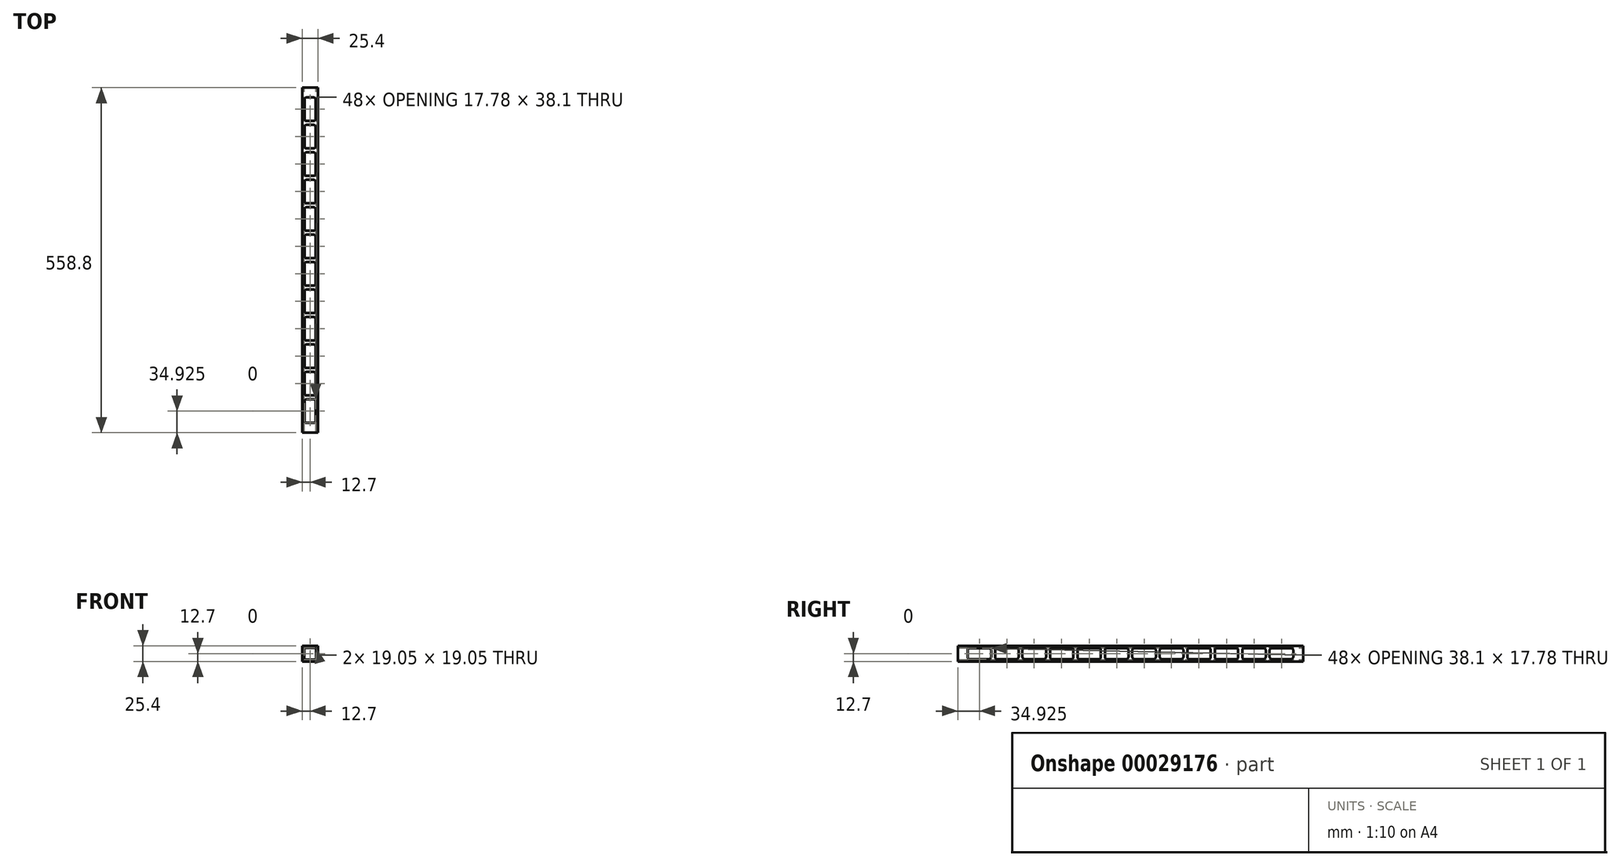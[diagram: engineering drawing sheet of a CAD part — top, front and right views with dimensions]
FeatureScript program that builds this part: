
annotation { "Feature Type Name" : "Feature", "Feature Type Description" : "" }
export const myFeature = defineFeature(function(context is Context, id is Id, definition is map)
    precondition{}
    {
        {
            var Q0;
            Q0=qCreatedBy(makeId("Front.planeOp"),FACE);
            var sketch = newSketch(context, id + "F0", { "sketchPlane" : qUnion([Q0])});
            skLineSegment(sketch, "E0.rect.bottom", {"start": v(12.7, 12.7) * mm, "end": v(-12.7, 12.7) * mm});
            skLineSegment(sketch, "E0.rect.top", {"start": v(12.7, -12.7) * mm, "end": v(-12.7, -12.7) * mm});
            skLineSegment(sketch, "E0.rect.left", {"start": v(12.7, 12.7) * mm, "end": v(12.7, -12.7) * mm});
            skLineSegment(sketch, "E0.rect.right", {"start": v(-12.7, 12.7) * mm, "end": v(-12.7, -12.7) * mm});
            skPoint(sketch, "E0.rect.middle", {"position": v(0, 0) * mm});
            skLineSegment(sketch, "E1.rect.bottom", {"start": v(9.53, 9.53) * mm, "end": v(-9.53, 9.53) * mm});
            skLineSegment(sketch, "E1.rect.top", {"start": v(9.53, -9.53) * mm, "end": v(-9.53, -9.53) * mm});
            skLineSegment(sketch, "E1.rect.left", {"start": v(9.53, 9.53) * mm, "end": v(9.53, -9.53) * mm});
            skLineSegment(sketch, "E1.rect.right", {"start": v(-9.53, 9.53) * mm, "end": v(-9.53, -9.53) * mm});
            skSolve(sketch);
        }
        {
            var Q0;
            Q0=qSketchRegion(id+"F0",true);
            extrude(context, id + "F1", {"entities" : qUnion([Q0]), "depth" : 558.8 * mm});
        }
        {
            var Q0;
            Q0=makeQuery(id+"F1.opExtrude","SWEPT_FACE",FACE,{"disambiguationData":[OSD([sQuery(id+"F0.wireOp",EDGE,"E0.rect.left")])]});
            var sketch = newSketch(context, id + "F2", { "sketchPlane" : qUnion([Q0])});
            skLineSegment(sketch, "E2", {"start": v(-558.8, 0) * mm, "end": v(-542.93, 0) * mm});
            skLineSegment(sketch, "E3.rect.bottom", {"start": v(-508, 8.89) * mm, "end": v(-539.75, 8.89) * mm});
            skLineSegment(sketch, "E3.rect.top", {"start": v(-508, -8.9) * mm, "end": v(-539.75, -8.9) * mm});
            skLineSegment(sketch, "E3.rect.left", {"start": v(-504.83, 5.71) * mm, "end": v(-504.83, -5.72) * mm});
            skLineSegment(sketch, "E3.rect.right", {"start": v(-542.93, 5.71) * mm, "end": v(-542.93, -5.72) * mm});
            skPoint(sketch, "E3.rect.middle", {"position": v(-523.88, 0) * mm});
            skPoint(sketch, "E4.visualSharp", {"position": v(-504.83, 8.89) * mm});
            skArc(sketch, "E4.filletArc", {"start": v(-504.83, 5.71) * mm, "mid": v(-505.75, 7.96) * mm, "end": v(-508, 8.89) * mm});
            skPoint(sketch, "E5.visualSharp", {"position": v(-504.83, -8.9) * mm});
            skArc(sketch, "E5.filletArc", {"start": v(-508, -8.9) * mm, "mid": v(-505.75, -7.96) * mm, "end": v(-504.82, -5.72) * mm});
            skPoint(sketch, "E6.visualSharp", {"position": v(-542.93, -8.9) * mm});
            skArc(sketch, "E6.filletArc", {"start": v(-542.93, -5.72) * mm, "mid": v(-542, -7.96) * mm, "end": v(-539.75, -8.9) * mm});
            skPoint(sketch, "E7.visualSharp", {"position": v(-542.93, 8.89) * mm});
            skArc(sketch, "E7.filletArc", {"start": v(-539.75, 8.9) * mm, "mid": v(-542, 7.96) * mm, "end": v(-542.93, 5.71) * mm});
            skLineSegment(sketch, "E8.1.0.0", {"start": v(-460.38, 5.71) * mm, "end": v(-460.38, -5.72) * mm});
            skArc(sketch, "E8.1.0.1", {"start": v(-460.38, 5.71) * mm, "mid": v(-461.3, 7.96) * mm, "end": v(-463.55, 8.89) * mm});
            skLineSegment(sketch, "E8.1.0.2", {"start": v(-463.55, 8.89) * mm, "end": v(-495.3, 8.89) * mm});
            skArc(sketch, "E8.1.0.3", {"start": v(-495.3, 8.9) * mm, "mid": v(-497.55, 7.96) * mm, "end": v(-498.48, 5.71) * mm});
            skLineSegment(sketch, "E8.1.0.4", {"start": v(-498.48, 5.71) * mm, "end": v(-498.48, -5.72) * mm});
            skArc(sketch, "E8.1.0.5", {"start": v(-498.48, -5.72) * mm, "mid": v(-497.55, -7.96) * mm, "end": v(-495.3, -8.9) * mm});
            skLineSegment(sketch, "E8.1.0.6", {"start": v(-463.55, -8.9) * mm, "end": v(-495.3, -8.9) * mm});
            skArc(sketch, "E8.1.0.7", {"start": v(-463.55, -8.9) * mm, "mid": v(-461.3, -7.96) * mm, "end": v(-460.38, -5.72) * mm});
            skLineSegment(sketch, "E8.2.0.0", {"start": v(-415.93, 5.71) * mm, "end": v(-415.93, -5.72) * mm});
            skArc(sketch, "E8.2.0.1", {"start": v(-415.93, 5.71) * mm, "mid": v(-416.85, 7.96) * mm, "end": v(-419.1, 8.89) * mm});
            skLineSegment(sketch, "E8.2.0.2", {"start": v(-419.1, 8.89) * mm, "end": v(-450.85, 8.89) * mm});
            skArc(sketch, "E8.2.0.3", {"start": v(-450.85, 8.9) * mm, "mid": v(-453.1, 7.96) * mm, "end": v(-454.03, 5.71) * mm});
            skLineSegment(sketch, "E8.2.0.4", {"start": v(-454.03, 5.71) * mm, "end": v(-454.03, -5.72) * mm});
            skArc(sketch, "E8.2.0.5", {"start": v(-454.03, -5.72) * mm, "mid": v(-453.1, -7.96) * mm, "end": v(-450.85, -8.9) * mm});
            skLineSegment(sketch, "E8.2.0.6", {"start": v(-419.1, -8.9) * mm, "end": v(-450.85, -8.9) * mm});
            skArc(sketch, "E8.2.0.7", {"start": v(-419.1, -8.9) * mm, "mid": v(-416.85, -7.96) * mm, "end": v(-415.93, -5.72) * mm});
            skLineSegment(sketch, "E8.3.0.0", {"start": v(-371.48, 5.71) * mm, "end": v(-371.48, -5.72) * mm});
            skArc(sketch, "E8.3.0.1", {"start": v(-371.48, 5.71) * mm, "mid": v(-372.4, 7.96) * mm, "end": v(-374.65, 8.89) * mm});
            skLineSegment(sketch, "E8.3.0.2", {"start": v(-374.65, 8.89) * mm, "end": v(-406.4, 8.89) * mm});
            skArc(sketch, "E8.3.0.3", {"start": v(-406.4, 8.9) * mm, "mid": v(-408.65, 7.96) * mm, "end": v(-409.58, 5.71) * mm});
            skLineSegment(sketch, "E8.3.0.4", {"start": v(-409.58, 5.71) * mm, "end": v(-409.58, -5.72) * mm});
            skArc(sketch, "E8.3.0.5", {"start": v(-409.58, -5.72) * mm, "mid": v(-408.65, -7.96) * mm, "end": v(-406.4, -8.9) * mm});
            skLineSegment(sketch, "E8.3.0.6", {"start": v(-374.65, -8.9) * mm, "end": v(-406.4, -8.9) * mm});
            skArc(sketch, "E8.3.0.7", {"start": v(-374.65, -8.9) * mm, "mid": v(-372.4, -7.96) * mm, "end": v(-371.48, -5.72) * mm});
            skLineSegment(sketch, "E8.4.0.0", {"start": v(-327.03, 5.71) * mm, "end": v(-327.03, -5.72) * mm});
            skArc(sketch, "E8.4.0.1", {"start": v(-327.03, 5.71) * mm, "mid": v(-327.95, 7.96) * mm, "end": v(-330.2, 8.89) * mm});
            skLineSegment(sketch, "E8.4.0.2", {"start": v(-330.2, 8.89) * mm, "end": v(-361.95, 8.89) * mm});
            skArc(sketch, "E8.4.0.3", {"start": v(-361.95, 8.9) * mm, "mid": v(-364.2, 7.96) * mm, "end": v(-365.13, 5.71) * mm});
            skLineSegment(sketch, "E8.4.0.4", {"start": v(-365.13, 5.71) * mm, "end": v(-365.13, -5.72) * mm});
            skArc(sketch, "E8.4.0.5", {"start": v(-365.13, -5.72) * mm, "mid": v(-364.2, -7.96) * mm, "end": v(-361.95, -8.9) * mm});
            skLineSegment(sketch, "E8.4.0.6", {"start": v(-330.2, -8.9) * mm, "end": v(-361.95, -8.9) * mm});
            skArc(sketch, "E8.4.0.7", {"start": v(-330.2, -8.9) * mm, "mid": v(-327.95, -7.96) * mm, "end": v(-327.03, -5.72) * mm});
            skLineSegment(sketch, "E8.5.0.0", {"start": v(-282.58, 5.71) * mm, "end": v(-282.58, -5.72) * mm});
            skArc(sketch, "E8.5.0.1", {"start": v(-282.58, 5.71) * mm, "mid": v(-283.5, 7.96) * mm, "end": v(-285.75, 8.89) * mm});
            skLineSegment(sketch, "E8.5.0.2", {"start": v(-285.75, 8.89) * mm, "end": v(-317.5, 8.89) * mm});
            skArc(sketch, "E8.5.0.3", {"start": v(-317.5, 8.9) * mm, "mid": v(-319.75, 7.96) * mm, "end": v(-320.68, 5.71) * mm});
            skLineSegment(sketch, "E8.5.0.4", {"start": v(-320.68, 5.71) * mm, "end": v(-320.68, -5.72) * mm});
            skArc(sketch, "E8.5.0.5", {"start": v(-320.68, -5.72) * mm, "mid": v(-319.75, -7.96) * mm, "end": v(-317.5, -8.9) * mm});
            skLineSegment(sketch, "E8.5.0.6", {"start": v(-285.75, -8.9) * mm, "end": v(-317.5, -8.9) * mm});
            skArc(sketch, "E8.5.0.7", {"start": v(-285.75, -8.9) * mm, "mid": v(-283.5, -7.96) * mm, "end": v(-282.58, -5.72) * mm});
            skLineSegment(sketch, "E8.6.0.0", {"start": v(-238.13, 5.71) * mm, "end": v(-238.13, -5.72) * mm});
            skArc(sketch, "E8.6.0.1", {"start": v(-238.13, 5.71) * mm, "mid": v(-239.05, 7.96) * mm, "end": v(-241.3, 8.89) * mm});
            skLineSegment(sketch, "E8.6.0.2", {"start": v(-241.3, 8.89) * mm, "end": v(-273.05, 8.89) * mm});
            skArc(sketch, "E8.6.0.3", {"start": v(-273.05, 8.9) * mm, "mid": v(-275.3, 7.96) * mm, "end": v(-276.23, 5.71) * mm});
            skLineSegment(sketch, "E8.6.0.4", {"start": v(-276.23, 5.71) * mm, "end": v(-276.23, -5.72) * mm});
            skArc(sketch, "E8.6.0.5", {"start": v(-276.23, -5.72) * mm, "mid": v(-275.3, -7.96) * mm, "end": v(-273.05, -8.9) * mm});
            skLineSegment(sketch, "E8.6.0.6", {"start": v(-241.3, -8.9) * mm, "end": v(-273.05, -8.9) * mm});
            skArc(sketch, "E8.6.0.7", {"start": v(-241.3, -8.9) * mm, "mid": v(-239.05, -7.96) * mm, "end": v(-238.13, -5.72) * mm});
            skLineSegment(sketch, "E8.7.0.0", {"start": v(-193.68, 5.71) * mm, "end": v(-193.68, -5.72) * mm});
            skArc(sketch, "E8.7.0.1", {"start": v(-193.68, 5.71) * mm, "mid": v(-194.6, 7.96) * mm, "end": v(-196.85, 8.89) * mm});
            skLineSegment(sketch, "E8.7.0.2", {"start": v(-196.85, 8.89) * mm, "end": v(-228.6, 8.89) * mm});
            skArc(sketch, "E8.7.0.3", {"start": v(-228.6, 8.9) * mm, "mid": v(-230.85, 7.96) * mm, "end": v(-231.78, 5.71) * mm});
            skLineSegment(sketch, "E8.7.0.4", {"start": v(-231.78, 5.71) * mm, "end": v(-231.78, -5.72) * mm});
            skArc(sketch, "E8.7.0.5", {"start": v(-231.78, -5.72) * mm, "mid": v(-230.85, -7.96) * mm, "end": v(-228.6, -8.9) * mm});
            skLineSegment(sketch, "E8.7.0.6", {"start": v(-196.85, -8.9) * mm, "end": v(-228.6, -8.9) * mm});
            skArc(sketch, "E8.7.0.7", {"start": v(-196.85, -8.9) * mm, "mid": v(-194.6, -7.96) * mm, "end": v(-193.68, -5.72) * mm});
            skLineSegment(sketch, "E8.8.0.0", {"start": v(-149.23, 5.71) * mm, "end": v(-149.23, -5.72) * mm});
            skArc(sketch, "E8.8.0.1", {"start": v(-149.23, 5.71) * mm, "mid": v(-150.15, 7.96) * mm, "end": v(-152.4, 8.89) * mm});
            skLineSegment(sketch, "E8.8.0.2", {"start": v(-152.4, 8.89) * mm, "end": v(-184.15, 8.89) * mm});
            skArc(sketch, "E8.8.0.3", {"start": v(-184.15, 8.9) * mm, "mid": v(-186.4, 7.96) * mm, "end": v(-187.33, 5.71) * mm});
            skLineSegment(sketch, "E8.8.0.4", {"start": v(-187.33, 5.71) * mm, "end": v(-187.33, -5.72) * mm});
            skArc(sketch, "E8.8.0.5", {"start": v(-187.33, -5.72) * mm, "mid": v(-186.4, -7.96) * mm, "end": v(-184.15, -8.9) * mm});
            skLineSegment(sketch, "E8.8.0.6", {"start": v(-152.4, -8.9) * mm, "end": v(-184.15, -8.9) * mm});
            skArc(sketch, "E8.8.0.7", {"start": v(-152.4, -8.9) * mm, "mid": v(-150.15, -7.96) * mm, "end": v(-149.23, -5.72) * mm});
            skLineSegment(sketch, "E8.direction1", {"start": v(-504.83, -5.72) * mm, "end": v(-460.38, -5.72) * mm, "construction": true});
            skLineSegment(sketch, "E9.0.9.0", {"start": v(-104.78, 5.71) * mm, "end": v(-104.78, -5.72) * mm});
            skArc(sketch, "E9.3.9.0", {"start": v(-104.78, 5.71) * mm, "mid": v(-105.7, 7.96) * mm, "end": v(-107.95, 8.89) * mm});
            skLineSegment(sketch, "E9.7.9.0", {"start": v(-107.95, 8.89) * mm, "end": v(-139.7, 8.89) * mm});
            skArc(sketch, "E9.10.9.0", {"start": v(-139.7, 8.9) * mm, "mid": v(-141.95, 7.96) * mm, "end": v(-142.88, 5.71) * mm});
            skLineSegment(sketch, "E9.14.9.0", {"start": v(-142.88, 5.71) * mm, "end": v(-142.88, -5.72) * mm});
            skArc(sketch, "E9.17.9.0", {"start": v(-142.88, -5.72) * mm, "mid": v(-141.95, -7.96) * mm, "end": v(-139.7, -8.9) * mm});
            skLineSegment(sketch, "E9.21.9.0", {"start": v(-107.95, -8.9) * mm, "end": v(-139.7, -8.9) * mm});
            skArc(sketch, "E9.24.9.0", {"start": v(-107.95, -8.9) * mm, "mid": v(-105.7, -7.96) * mm, "end": v(-104.78, -5.72) * mm});
            skLineSegment(sketch, "E9.0.10.0", {"start": v(-60.33, 5.71) * mm, "end": v(-60.33, -5.72) * mm});
            skArc(sketch, "E9.3.10.0", {"start": v(-60.33, 5.71) * mm, "mid": v(-61.25, 7.96) * mm, "end": v(-63.5, 8.89) * mm});
            skLineSegment(sketch, "E9.7.10.0", {"start": v(-63.5, 8.89) * mm, "end": v(-95.25, 8.89) * mm});
            skArc(sketch, "E9.10.10.0", {"start": v(-95.25, 8.9) * mm, "mid": v(-97.5, 7.96) * mm, "end": v(-98.43, 5.71) * mm});
            skLineSegment(sketch, "E9.14.10.0", {"start": v(-98.43, 5.71) * mm, "end": v(-98.43, -5.72) * mm});
            skArc(sketch, "E9.17.10.0", {"start": v(-98.43, -5.72) * mm, "mid": v(-97.5, -7.96) * mm, "end": v(-95.25, -8.9) * mm});
            skLineSegment(sketch, "E9.21.10.0", {"start": v(-63.5, -8.9) * mm, "end": v(-95.25, -8.9) * mm});
            skArc(sketch, "E9.24.10.0", {"start": v(-63.5, -8.9) * mm, "mid": v(-61.25, -7.96) * mm, "end": v(-60.33, -5.72) * mm});
            skLineSegment(sketch, "E10.0.11.0", {"start": v(-15.88, 5.71) * mm, "end": v(-15.88, -5.72) * mm});
            skArc(sketch, "E10.3.11.0", {"start": v(-15.88, 5.71) * mm, "mid": v(-16.8, 7.96) * mm, "end": v(-19.05, 8.89) * mm});
            skLineSegment(sketch, "E10.7.11.0", {"start": v(-19.05, 8.89) * mm, "end": v(-50.8, 8.89) * mm});
            skArc(sketch, "E10.10.11.0", {"start": v(-50.8, 8.9) * mm, "mid": v(-53.05, 7.96) * mm, "end": v(-53.98, 5.71) * mm});
            skLineSegment(sketch, "E10.14.11.0", {"start": v(-53.98, 5.71) * mm, "end": v(-53.98, -5.72) * mm});
            skArc(sketch, "E10.17.11.0", {"start": v(-53.98, -5.72) * mm, "mid": v(-53.05, -7.96) * mm, "end": v(-50.8, -8.9) * mm});
            skLineSegment(sketch, "E10.21.11.0", {"start": v(-19.05, -8.9) * mm, "end": v(-50.8, -8.9) * mm});
            skArc(sketch, "E10.24.11.0", {"start": v(-19.05, -8.9) * mm, "mid": v(-16.8, -7.96) * mm, "end": v(-15.88, -5.72) * mm});
            skLineSegment(sketch, "E11.trimOffspring", {"start": v(-504.83, 0) * mm, "end": v(0, 0) * mm});
            skSolve(sketch);
        }
        {
            var Q0;
            Q0 = qSketchRegion(id + "F2", true);
            extrude(context, id + "F3", {"entities" : qUnion([Q0]), "operationType" : NewBodyOperationType.REMOVE, "oppositeDirection" : true, "depth" : 25.4 * mm});
        }
        {
            var Q0;
            Q0=makeQuery(id+"F1.opExtrude","SWEPT_FACE",FACE,{"disambiguationData":[OSD([sQuery(id+"F0.wireOp",EDGE,"E0.rect.bottom")])]});
            var sketch = newSketch(context, id + "F4", { "sketchPlane" : qUnion([Q0])});
            skLineSegment(sketch, "E12", {"start": v(0, -558.8) * mm, "end": v(0, 0) * mm});
            skLineSegment(sketch, "E13.rect.bottom", {"start": v(5.72, -504.83) * mm, "end": v(-5.71, -504.83) * mm});
            skLineSegment(sketch, "E13.rect.top", {"start": v(5.72, -542.93) * mm, "end": v(-5.71, -542.93) * mm});
            skLineSegment(sketch, "E13.rect.left", {"start": v(8.9, -508) * mm, "end": v(8.9, -539.75) * mm});
            skLineSegment(sketch, "E13.rect.right", {"start": v(-8.89, -508) * mm, "end": v(-8.89, -539.75) * mm});
            skPoint(sketch, "E13.rect.middle", {"position": v(0, -523.88) * mm});
            skPoint(sketch, "E14.visualSharp", {"position": v(-8.89, -504.83) * mm});
            skArc(sketch, "E14.filletArc", {"start": v(-5.71, -504.83) * mm, "mid": v(-7.96, -505.75) * mm, "end": v(-8.89, -508) * mm});
            skPoint(sketch, "E15.visualSharp", {"position": v(8.9, -542.93) * mm});
            skArc(sketch, "E15.filletArc", {"start": v(5.72, -542.93) * mm, "mid": v(7.96, -542) * mm, "end": v(8.9, -539.75) * mm});
            skPoint(sketch, "E16.visualSharp", {"position": v(-8.89, -542.93) * mm});
            skArc(sketch, "E16.filletArc", {"start": v(-8.9, -539.75) * mm, "mid": v(-7.96, -542) * mm, "end": v(-5.71, -542.93) * mm});
            skPoint(sketch, "E17.visualSharp", {"position": v(8.9, -504.83) * mm});
            skArc(sketch, "E17.filletArc", {"start": v(8.9, -508) * mm, "mid": v(7.96, -505.75) * mm, "end": v(5.72, -504.82) * mm});
            skLineSegment(sketch, "E18.0.1.0", {"start": v(5.72, -460.38) * mm, "end": v(-5.71, -460.38) * mm});
            skArc(sketch, "E18.0.1.1", {"start": v(-5.71, -460.38) * mm, "mid": v(-7.96, -461.3) * mm, "end": v(-8.89, -463.55) * mm});
            skLineSegment(sketch, "E18.0.1.2", {"start": v(-8.89, -463.55) * mm, "end": v(-8.89, -495.3) * mm});
            skArc(sketch, "E18.0.1.3", {"start": v(-8.9, -495.3) * mm, "mid": v(-7.96, -497.55) * mm, "end": v(-5.71, -498.48) * mm});
            skLineSegment(sketch, "E18.0.1.4", {"start": v(5.72, -498.48) * mm, "end": v(-5.71, -498.48) * mm});
            skArc(sketch, "E18.0.1.5", {"start": v(5.72, -498.48) * mm, "mid": v(7.96, -497.55) * mm, "end": v(8.9, -495.3) * mm});
            skLineSegment(sketch, "E18.0.1.6", {"start": v(8.9, -463.55) * mm, "end": v(8.9, -495.3) * mm});
            skArc(sketch, "E18.0.1.7", {"start": v(8.9, -463.55) * mm, "mid": v(7.96, -461.3) * mm, "end": v(5.72, -460.38) * mm});
            skLineSegment(sketch, "E18.0.2.0", {"start": v(5.72, -415.93) * mm, "end": v(-5.71, -415.93) * mm});
            skArc(sketch, "E18.0.2.1", {"start": v(-5.71, -415.93) * mm, "mid": v(-7.96, -416.85) * mm, "end": v(-8.89, -419.1) * mm});
            skLineSegment(sketch, "E18.0.2.2", {"start": v(-8.89, -419.1) * mm, "end": v(-8.89, -450.85) * mm});
            skArc(sketch, "E18.0.2.3", {"start": v(-8.9, -450.85) * mm, "mid": v(-7.96, -453.1) * mm, "end": v(-5.71, -454.03) * mm});
            skLineSegment(sketch, "E18.0.2.4", {"start": v(5.72, -454.03) * mm, "end": v(-5.71, -454.03) * mm});
            skArc(sketch, "E18.0.2.5", {"start": v(5.72, -454.03) * mm, "mid": v(7.96, -453.1) * mm, "end": v(8.9, -450.85) * mm});
            skLineSegment(sketch, "E18.0.2.6", {"start": v(8.9, -419.1) * mm, "end": v(8.9, -450.85) * mm});
            skArc(sketch, "E18.0.2.7", {"start": v(8.9, -419.1) * mm, "mid": v(7.96, -416.85) * mm, "end": v(5.72, -415.93) * mm});
            skLineSegment(sketch, "E18.0.3.0", {"start": v(5.72, -371.48) * mm, "end": v(-5.71, -371.48) * mm});
            skArc(sketch, "E18.0.3.1", {"start": v(-5.71, -371.48) * mm, "mid": v(-7.96, -372.4) * mm, "end": v(-8.89, -374.65) * mm});
            skLineSegment(sketch, "E18.0.3.2", {"start": v(-8.89, -374.65) * mm, "end": v(-8.89, -406.4) * mm});
            skArc(sketch, "E18.0.3.3", {"start": v(-8.9, -406.4) * mm, "mid": v(-7.96, -408.65) * mm, "end": v(-5.71, -409.58) * mm});
            skLineSegment(sketch, "E18.0.3.4", {"start": v(5.72, -409.58) * mm, "end": v(-5.71, -409.58) * mm});
            skArc(sketch, "E18.0.3.5", {"start": v(5.72, -409.58) * mm, "mid": v(7.96, -408.65) * mm, "end": v(8.9, -406.4) * mm});
            skLineSegment(sketch, "E18.0.3.6", {"start": v(8.9, -374.65) * mm, "end": v(8.9, -406.4) * mm});
            skArc(sketch, "E18.0.3.7", {"start": v(8.9, -374.65) * mm, "mid": v(7.96, -372.4) * mm, "end": v(5.72, -371.48) * mm});
            skLineSegment(sketch, "E18.0.4.0", {"start": v(5.72, -327.03) * mm, "end": v(-5.71, -327.03) * mm});
            skArc(sketch, "E18.0.4.1", {"start": v(-5.71, -327.03) * mm, "mid": v(-7.96, -327.95) * mm, "end": v(-8.89, -330.2) * mm});
            skLineSegment(sketch, "E18.0.4.2", {"start": v(-8.89, -330.2) * mm, "end": v(-8.89, -361.95) * mm});
            skArc(sketch, "E18.0.4.3", {"start": v(-8.9, -361.95) * mm, "mid": v(-7.96, -364.2) * mm, "end": v(-5.71, -365.13) * mm});
            skLineSegment(sketch, "E18.0.4.4", {"start": v(5.72, -365.13) * mm, "end": v(-5.71, -365.13) * mm});
            skArc(sketch, "E18.0.4.5", {"start": v(5.72, -365.13) * mm, "mid": v(7.96, -364.2) * mm, "end": v(8.9, -361.95) * mm});
            skLineSegment(sketch, "E18.0.4.6", {"start": v(8.9, -330.2) * mm, "end": v(8.9, -361.95) * mm});
            skArc(sketch, "E18.0.4.7", {"start": v(8.9, -330.2) * mm, "mid": v(7.96, -327.95) * mm, "end": v(5.72, -327.03) * mm});
            skLineSegment(sketch, "E18.0.5.0", {"start": v(5.72, -282.58) * mm, "end": v(-5.71, -282.58) * mm});
            skArc(sketch, "E18.0.5.1", {"start": v(-5.71, -282.58) * mm, "mid": v(-7.96, -283.5) * mm, "end": v(-8.89, -285.75) * mm});
            skLineSegment(sketch, "E18.0.5.2", {"start": v(-8.89, -285.75) * mm, "end": v(-8.89, -317.5) * mm});
            skArc(sketch, "E18.0.5.3", {"start": v(-8.9, -317.5) * mm, "mid": v(-7.96, -319.75) * mm, "end": v(-5.71, -320.68) * mm});
            skLineSegment(sketch, "E18.0.5.4", {"start": v(5.72, -320.68) * mm, "end": v(-5.71, -320.68) * mm});
            skArc(sketch, "E18.0.5.5", {"start": v(5.72, -320.68) * mm, "mid": v(7.96, -319.75) * mm, "end": v(8.9, -317.5) * mm});
            skLineSegment(sketch, "E18.0.5.6", {"start": v(8.9, -285.75) * mm, "end": v(8.9, -317.5) * mm});
            skArc(sketch, "E18.0.5.7", {"start": v(8.9, -285.75) * mm, "mid": v(7.96, -283.5) * mm, "end": v(5.72, -282.58) * mm});
            skLineSegment(sketch, "E18.0.6.0", {"start": v(5.72, -238.13) * mm, "end": v(-5.71, -238.13) * mm});
            skArc(sketch, "E18.0.6.1", {"start": v(-5.71, -238.13) * mm, "mid": v(-7.96, -239.05) * mm, "end": v(-8.89, -241.3) * mm});
            skLineSegment(sketch, "E18.0.6.2", {"start": v(-8.89, -241.3) * mm, "end": v(-8.89, -273.05) * mm});
            skArc(sketch, "E18.0.6.3", {"start": v(-8.9, -273.05) * mm, "mid": v(-7.96, -275.3) * mm, "end": v(-5.71, -276.23) * mm});
            skLineSegment(sketch, "E18.0.6.4", {"start": v(5.72, -276.23) * mm, "end": v(-5.71, -276.23) * mm});
            skArc(sketch, "E18.0.6.5", {"start": v(5.72, -276.23) * mm, "mid": v(7.96, -275.3) * mm, "end": v(8.9, -273.05) * mm});
            skLineSegment(sketch, "E18.0.6.6", {"start": v(8.9, -241.3) * mm, "end": v(8.9, -273.05) * mm});
            skArc(sketch, "E18.0.6.7", {"start": v(8.9, -241.3) * mm, "mid": v(7.96, -239.05) * mm, "end": v(5.72, -238.13) * mm});
            skLineSegment(sketch, "E18.0.7.0", {"start": v(5.72, -193.68) * mm, "end": v(-5.71, -193.68) * mm});
            skArc(sketch, "E18.0.7.1", {"start": v(-5.71, -193.68) * mm, "mid": v(-7.96, -194.6) * mm, "end": v(-8.89, -196.85) * mm});
            skLineSegment(sketch, "E18.0.7.2", {"start": v(-8.89, -196.85) * mm, "end": v(-8.89, -228.6) * mm});
            skArc(sketch, "E18.0.7.3", {"start": v(-8.9, -228.6) * mm, "mid": v(-7.96, -230.85) * mm, "end": v(-5.71, -231.78) * mm});
            skLineSegment(sketch, "E18.0.7.4", {"start": v(5.72, -231.78) * mm, "end": v(-5.71, -231.78) * mm});
            skArc(sketch, "E18.0.7.5", {"start": v(5.72, -231.78) * mm, "mid": v(7.96, -230.85) * mm, "end": v(8.9, -228.6) * mm});
            skLineSegment(sketch, "E18.0.7.6", {"start": v(8.9, -196.85) * mm, "end": v(8.9, -228.6) * mm});
            skArc(sketch, "E18.0.7.7", {"start": v(8.9, -196.85) * mm, "mid": v(7.96, -194.6) * mm, "end": v(5.72, -193.68) * mm});
            skLineSegment(sketch, "E18.0.8.0", {"start": v(5.72, -149.23) * mm, "end": v(-5.71, -149.23) * mm});
            skArc(sketch, "E18.0.8.1", {"start": v(-5.71, -149.23) * mm, "mid": v(-7.96, -150.15) * mm, "end": v(-8.89, -152.4) * mm});
            skLineSegment(sketch, "E18.0.8.2", {"start": v(-8.89, -152.4) * mm, "end": v(-8.89, -184.15) * mm});
            skArc(sketch, "E18.0.8.3", {"start": v(-8.9, -184.15) * mm, "mid": v(-7.96, -186.4) * mm, "end": v(-5.71, -187.33) * mm});
            skLineSegment(sketch, "E18.0.8.4", {"start": v(5.72, -187.33) * mm, "end": v(-5.71, -187.33) * mm});
            skArc(sketch, "E18.0.8.5", {"start": v(5.72, -187.33) * mm, "mid": v(7.96, -186.4) * mm, "end": v(8.9, -184.15) * mm});
            skLineSegment(sketch, "E18.0.8.6", {"start": v(8.9, -152.4) * mm, "end": v(8.9, -184.15) * mm});
            skArc(sketch, "E18.0.8.7", {"start": v(8.9, -152.4) * mm, "mid": v(7.96, -150.15) * mm, "end": v(5.72, -149.23) * mm});
            skLineSegment(sketch, "E18.0.9.0", {"start": v(5.72, -104.78) * mm, "end": v(-5.71, -104.78) * mm});
            skArc(sketch, "E18.0.9.1", {"start": v(-5.71, -104.78) * mm, "mid": v(-7.96, -105.7) * mm, "end": v(-8.89, -107.95) * mm});
            skLineSegment(sketch, "E18.0.9.2", {"start": v(-8.89, -107.95) * mm, "end": v(-8.89, -139.7) * mm});
            skArc(sketch, "E18.0.9.3", {"start": v(-8.9, -139.7) * mm, "mid": v(-7.96, -141.95) * mm, "end": v(-5.71, -142.88) * mm});
            skLineSegment(sketch, "E18.0.9.4", {"start": v(5.72, -142.88) * mm, "end": v(-5.71, -142.88) * mm});
            skArc(sketch, "E18.0.9.5", {"start": v(5.72, -142.88) * mm, "mid": v(7.96, -141.95) * mm, "end": v(8.9, -139.7) * mm});
            skLineSegment(sketch, "E18.0.9.6", {"start": v(8.9, -107.95) * mm, "end": v(8.9, -139.7) * mm});
            skArc(sketch, "E18.0.9.7", {"start": v(8.9, -107.95) * mm, "mid": v(7.96, -105.7) * mm, "end": v(5.72, -104.78) * mm});
            skLineSegment(sketch, "E18.0.10.0", {"start": v(5.72, -60.33) * mm, "end": v(-5.71, -60.33) * mm});
            skArc(sketch, "E18.0.10.1", {"start": v(-5.71, -60.33) * mm, "mid": v(-7.96, -61.25) * mm, "end": v(-8.89, -63.5) * mm});
            skLineSegment(sketch, "E18.0.10.2", {"start": v(-8.89, -63.5) * mm, "end": v(-8.89, -95.25) * mm});
            skArc(sketch, "E18.0.10.3", {"start": v(-8.9, -95.25) * mm, "mid": v(-7.96, -97.5) * mm, "end": v(-5.71, -98.43) * mm});
            skLineSegment(sketch, "E18.0.10.4", {"start": v(5.72, -98.43) * mm, "end": v(-5.71, -98.43) * mm});
            skArc(sketch, "E18.0.10.5", {"start": v(5.72, -98.43) * mm, "mid": v(7.96, -97.5) * mm, "end": v(8.9, -95.25) * mm});
            skLineSegment(sketch, "E18.0.10.6", {"start": v(8.9, -63.5) * mm, "end": v(8.9, -95.25) * mm});
            skArc(sketch, "E18.0.10.7", {"start": v(8.9, -63.5) * mm, "mid": v(7.96, -61.25) * mm, "end": v(5.72, -60.33) * mm});
            skLineSegment(sketch, "E18.0.11.0", {"start": v(5.72, -15.88) * mm, "end": v(-5.71, -15.88) * mm});
            skArc(sketch, "E18.0.11.1", {"start": v(-5.71, -15.88) * mm, "mid": v(-7.96, -16.8) * mm, "end": v(-8.89, -19.05) * mm});
            skLineSegment(sketch, "E18.0.11.2", {"start": v(-8.89, -19.05) * mm, "end": v(-8.89, -50.8) * mm});
            skArc(sketch, "E18.0.11.3", {"start": v(-8.9, -50.8) * mm, "mid": v(-7.96, -53.05) * mm, "end": v(-5.71, -53.98) * mm});
            skLineSegment(sketch, "E18.0.11.4", {"start": v(5.72, -53.98) * mm, "end": v(-5.71, -53.98) * mm});
            skArc(sketch, "E18.0.11.5", {"start": v(5.72, -53.98) * mm, "mid": v(7.96, -53.05) * mm, "end": v(8.9, -50.8) * mm});
            skLineSegment(sketch, "E18.0.11.6", {"start": v(8.9, -19.05) * mm, "end": v(8.9, -50.8) * mm});
            skArc(sketch, "E18.0.11.7", {"start": v(8.9, -19.05) * mm, "mid": v(7.96, -16.8) * mm, "end": v(5.72, -15.88) * mm});
            skLineSegment(sketch, "E18.direction1", {"start": v(-5.71, -504.83) * mm, "end": v(19.69, -504.83) * mm, "construction": true});
            skLineSegment(sketch, "E18.direction2", {"start": v(-5.71, -504.83) * mm, "end": v(-5.71, -460.38) * mm, "construction": true});
            skSolve(sketch);
        }
        {
            var Q0;
            Q0 = qSketchRegion(id + "F4", true);
            extrude(context, id + "F5", {"entities" : qUnion([Q0]), "operationType" : NewBodyOperationType.REMOVE, "oppositeDirection" : true, "depth" : 25.4 * mm});
        }
    });
